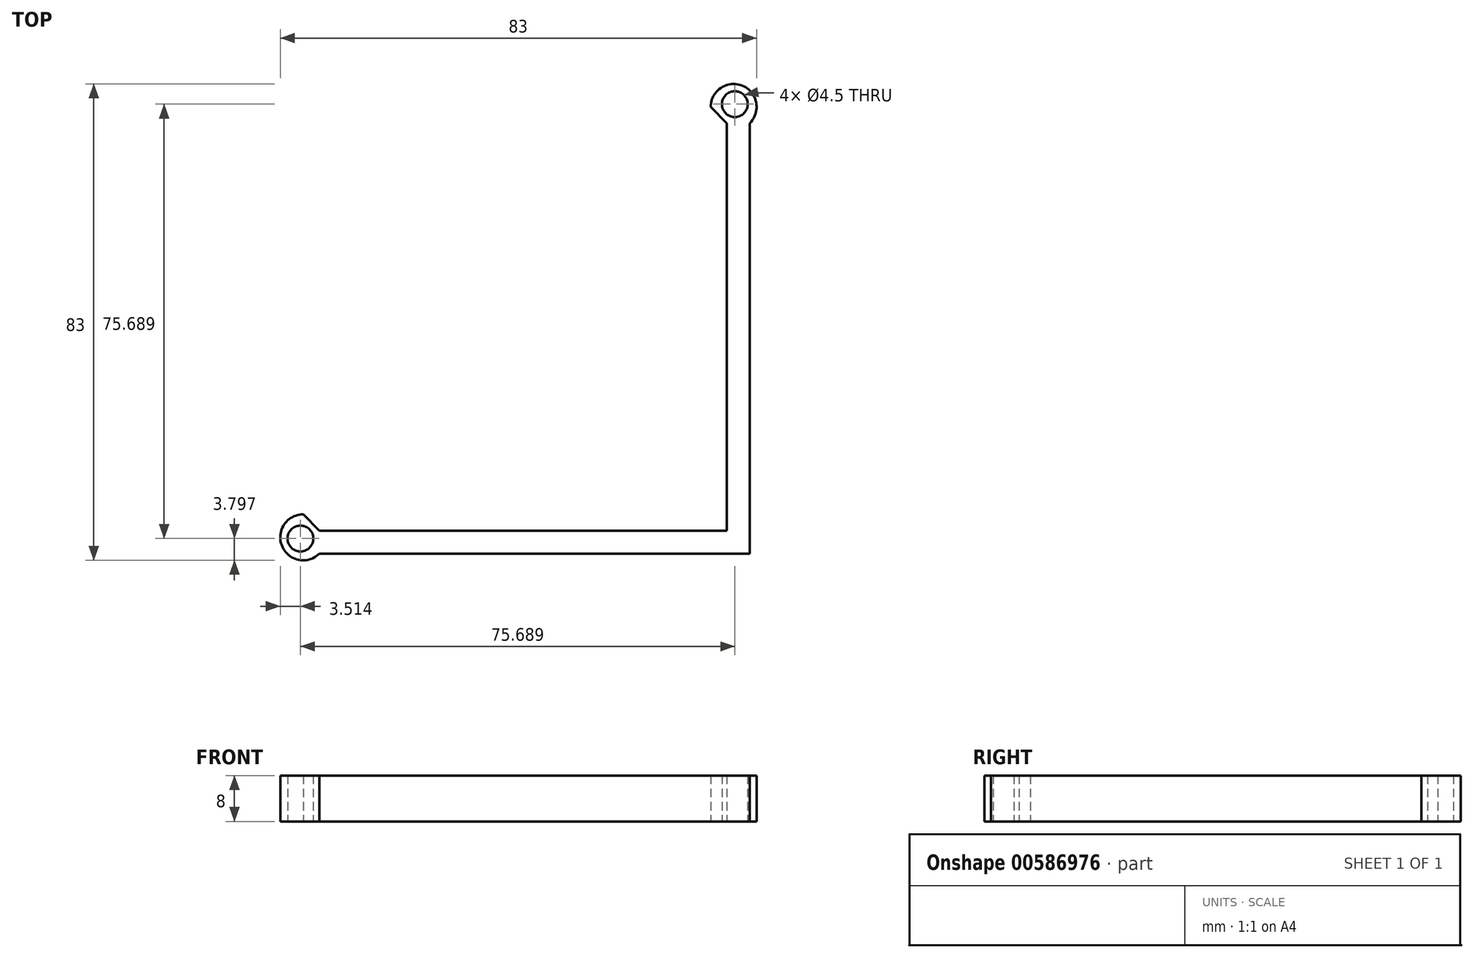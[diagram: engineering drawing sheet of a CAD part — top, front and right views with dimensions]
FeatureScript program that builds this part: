
annotation { "Feature Type Name" : "Feature", "Feature Type Description" : "" }
export const myFeature = defineFeature(function(context is Context, id is Id, definition is map)
    precondition{}
    {
        {
            var Q0;
            Q0=qCreatedBy(makeId("Top.planeOp"),FACE);
            var sketch = newSketch(context, id + "F0", { "sketchPlane" : qUnion([Q0])});
            skLineSegment(sketch, "E0.bottom", {"start": v(35.5, -35.5) * mm, "end": v(-35.5, -35.5) * mm});
            skLineSegment(sketch, "E0.top", {"start": v(35.5, 35.5) * mm, "end": v(-35.5, 35.5) * mm, "construction": true});
            skLineSegment(sketch, "E0.left", {"start": v(35.5, -35.5) * mm, "end": v(35.5, 35.5) * mm});
            skLineSegment(sketch, "E0.right", {"start": v(-35.5, -35.5) * mm, "end": v(-35.5, 35.5) * mm, "construction": true});
            skPoint(sketch, "E0.middle", {"position": v(0, 0) * mm});
            skLineSegment(sketch, "E1", {"start": v(-35.5, -35.5) * mm, "end": v(35.5, 35.5) * mm});
            skLineSegment(sketch, "E2.top", {"start": v(35.5, -39.5) * mm, "end": v(-35.5, -39.5) * mm});
            skLineSegment(sketch, "E2.left", {"start": v(35.5, -35.5) * mm, "end": v(35.5, -39.5) * mm, "construction": true});
            skLineSegment(sketch, "E2.right", {"start": v(-35.5, -35.5) * mm, "end": v(-35.5, -39.5) * mm});
            skLineSegment(sketch, "E3.bottom", {"start": v(35.5, -35.5) * mm, "end": v(39.5, -35.5) * mm});
            skLineSegment(sketch, "E3.top", {"start": v(35.5, 35.5) * mm, "end": v(39.5, 35.5) * mm});
            skLineSegment(sketch, "E3.right", {"start": v(39.5, -35.5) * mm, "end": v(39.5, 35.5) * mm});
            skLineSegment(sketch, "E4", {"start": v(-35.5, -35.5) * mm, "end": v(-38.33, -32.67) * mm});
            skLineSegment(sketch, "E5", {"start": v(35.5, 35.5) * mm, "end": v(32.67, 38.33) * mm});
            skLineSegment(sketch, "E6", {"start": v(32.67, 38.33) * mm, "end": v(-38.33, -32.67) * mm});
            skArc(sketch, "E7", {"start": v(39.5, 35.5) * mm, "mid": v(38.2, 42.02) * mm, "end": v(32.67, 38.33) * mm});
            skArc(sketch, "E8", {"start": v(-38.33, -32.67) * mm, "mid": v(-42.02, -38.2) * mm, "end": v(-35.5, -39.5) * mm});
            skLineSegment(sketch, "E9.top", {"start": v(35.5, -35.5) * mm, "end": v(33.5, -35.5) * mm});
            skLineSegment(sketch, "E9.left", {"start": v(35.5, -39.5) * mm, "end": v(35.5, -35.5) * mm});
            skLineSegment(sketch, "E9.right", {"start": v(33.5, -39.5) * mm, "end": v(33.5, -35.5) * mm, "construction": true});
            skLineSegment(sketch, "E10.bottom", {"start": v(39.5, -35.5) * mm, "end": v(35.5, -35.5) * mm});
            skLineSegment(sketch, "E10.top", {"start": v(39.5, -33.5) * mm, "end": v(35.5, -33.5) * mm});
            skLineSegment(sketch, "E10.left", {"start": v(39.5, -35.5) * mm, "end": v(39.5, -33.5) * mm});
            skLineSegment(sketch, "E10.right", {"start": v(35.5, -35.5) * mm, "end": v(35.5, -33.5) * mm});
            skLineSegment(sketch, "E11.bottom", {"start": v(35.5, -35.5) * mm, "end": v(38.25, -35.5) * mm});
            skLineSegment(sketch, "E11.left", {"start": v(35.5, -35.5) * mm, "end": v(35.5, -38.25) * mm});
            skLineSegment(sketch, "E12", {"start": v(-38.33, -32.67) * mm, "end": v(-38.82, -36.87) * mm});
            skLineSegment(sketch, "E13", {"start": v(-38.82, -36.87) * mm, "end": v(-35.5, -39.5) * mm});
            skCircle(sketch, "E14", {"center": v(-38.82, -36.87) * mm, "radius": 2.25 * mm});
            skLineSegment(sketch, "E15.top", {"start": v(35.5, -39.5) * mm, "end": v(39.5, -39.5) * mm});
            skLineSegment(sketch, "E15.left", {"start": v(35.5, -35.5) * mm, "end": v(35.5, -39.5) * mm});
            skLineSegment(sketch, "E15.right", {"start": v(39.5, -35.5) * mm, "end": v(39.5, -39.5) * mm});
            skLineSegment(sketch, "E16", {"start": v(32.67, 38.33) * mm, "end": v(36.87, 38.82) * mm});
            skLineSegment(sketch, "E17", {"start": v(36.87, 38.82) * mm, "end": v(39.5, 35.5) * mm});
            skCircle(sketch, "E18", {"center": v(36.87, 38.82) * mm, "radius": 2.25 * mm});
            skSolve(sketch);
        }
        {
            var Q0;
            {var subQ2=sQuery(id+"F0.wireOp",EDGE,"E2.right");Q0=makeQuery(id+"F0.imprint","IMPRINT",FACE,{"disambiguationData":[TD([[makeQuery(id+"F0.imprint","IMPRINT",EDGE,{"derivedFrom":subQ2}),-1.0]])]});}
            var Q1;
            {var subQ0=sQuery(id+"F0.wireOp",EDGE,"E8");Q1=makeQuery(id+"F0.imprint","IMPRINT",FACE,{"disambiguationData":[TD([[makeQuery(id+"F0.imprint","IMPRINT",EDGE,{"derivedFrom":subQ0}),1.0]])]});}
            var Q2;
            Q2=makeQuery(id+"F0.imprint","IMPRINT",FACE,{"disambiguationData":[TD([[makeQuery(id+"F0.imprint","IMPRINT",EDGE,{"derivedFrom":sQuery(id+"F0.wireOp",EDGE,"E0.bottom")}),1.0]])]});
            var Q3;
            {var subQ4=sQuery(id+"F0.wireOp",EDGE,"E15.top");Q3=makeQuery(id+"F0.imprint","IMPRINT",FACE,{"disambiguationData":[TD([[makeQuery(id+"F0.imprint","IMPRINT",EDGE,{"derivedFrom":subQ4}),1.0]])]});}
            var Q4;
            Q4=makeQuery(id+"F0.imprint","IMPRINT",FACE,{"disambiguationData":[TD([[makeQuery(id+"F0.imprint","IMPRINT",EDGE,{"derivedFrom":sQuery(id+"F0.wireOp",EDGE,"E10.top")}),1.0]])]});
            var Q5;
            Q5=makeQuery(id+"F0.imprint","IMPRINT",FACE,{"disambiguationData":[TD([[makeQuery(id+"F0.imprint","IMPRINT",EDGE,{"derivedFrom":sQuery(id+"F0.wireOp",EDGE,"E3.top")}),-1.0]])]});
            var Q6;
            {var subQ2=sQuery(id+"F0.wireOp",EDGE,"E3.top");Q6=makeQuery(id+"F0.imprint","IMPRINT",FACE,{"disambiguationData":[TD([[makeQuery(id+"F0.imprint","IMPRINT",EDGE,{"derivedFrom":subQ2}),1.0]])]});}
            var Q7;
            {var subQ0=sQuery(id+"F0.wireOp",EDGE,"E7");Q7=makeQuery(id+"F0.imprint","IMPRINT",FACE,{"disambiguationData":[TD([[makeQuery(id+"F0.imprint","IMPRINT",EDGE,{"derivedFrom":subQ0}),1.0]])]});}
            extrude(context, id + "F1", {"entities" : qUnion([Q0, Q1, Q2, Q3, Q4, Q5, Q6, Q7]), "depth" : 8 * mm, "offsetDistance" : 25 * mm});
        }
    });
